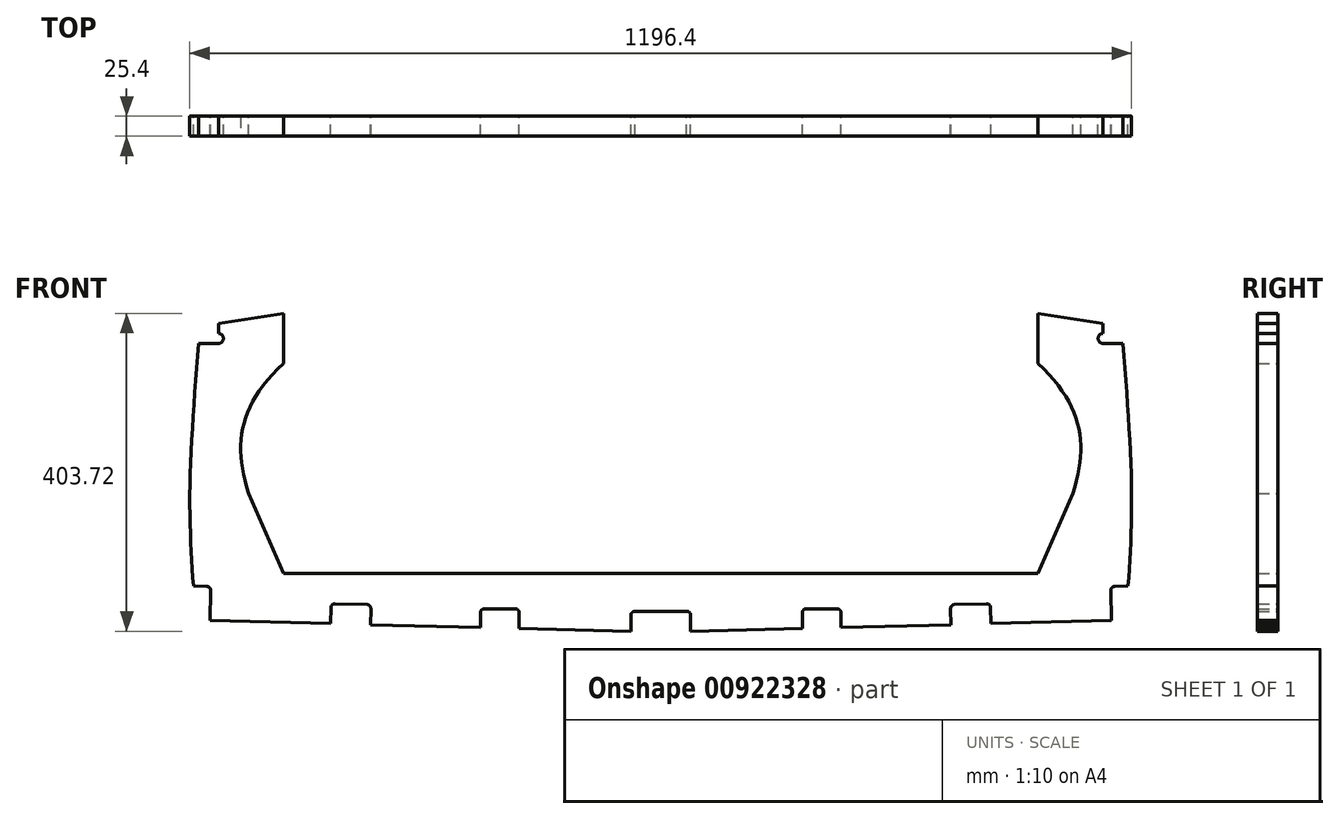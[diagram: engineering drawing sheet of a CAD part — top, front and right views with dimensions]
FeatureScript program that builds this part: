
annotation { "Feature Type Name" : "Feature", "Feature Type Description" : "" }
export const myFeature = defineFeature(function(context is Context, id is Id, definition is map)
    precondition{}
    {
        {
            var Q0;
            Q0=qCreatedBy(makeId("Front.planeOp"),FACE);
            var sketch = newSketch(context, id + "F0", { "sketchPlane" : qUnion([Q0])});
            skLineSegment(sketch, "E0", {"start": v(-38, -73.52) * mm, "end": v(-180.28, -69.8) * mm});
            skLineSegment(sketch, "E1", {"start": v(-180.28, -69.8) * mm, "end": v(-179.77, -50.34) * mm});
            skLineSegment(sketch, "E2", {"start": v(-184.85, -45.12) * mm, "end": v(-224.05, -45.12) * mm});
            skLineSegment(sketch, "E3", {"start": v(-229.13, -50.2) * mm, "end": v(-229.13, -68.9) * mm});
            skLineSegment(sketch, "E4", {"start": v(-229.13, -68.9) * mm, "end": v(-368.78, -65.22) * mm});
            skLineSegment(sketch, "E5", {"start": v(-368.78, -65.22) * mm, "end": v(-368.24, -44.91) * mm});
            skLineSegment(sketch, "E6", {"start": v(-373.19, -39.7) * mm, "end": v(-413.82, -38.63) * mm});
            skLineSegment(sketch, "E7", {"start": v(-419.03, -43.58) * mm, "end": v(-419.56, -63.89) * mm});
            skLineSegment(sketch, "E8", {"start": v(-572.7, -59.86) * mm, "end": v(-571.7, -21.77) * mm});
            skLineSegment(sketch, "E9", {"start": v(-576.65, -16.56) * mm, "end": v(-593.66, -16.11) * mm});
            skLineSegment(sketch, "E10", {"start": v(-561.9, 317.5) * mm, "end": v(-479.35, 330.2) * mm});
            skLineSegment(sketch, "E11", {"start": v(-479.35, 330.2) * mm, "end": v(-479.35, 266.6) * mm});
            skLineSegment(sketch, "E12", {"start": v(-479.35, 0) * mm, "end": v(-523.8, 101.6) * mm});
            skLineSegment(sketch, "E13", {"start": v(-561.9, 292.1) * mm, "end": v(-587.3, 292.1) * mm});
            skFitSpline(sketch, "E14", {"points": [v(-479.35, 266.6) * mm, v(-523.8, 101.6) * mm], "startDerivative": vector(-173.65, -164.2) * mm, "endDerivative": vector(56.39, -189.22) * mm});
            skLineSegment(sketch, "E15", {"start": v(-479.35, 0) * mm, "end": v(0, 0) * mm});
            skLineSegment(sketch, "E16", {"start": v(-572.7, -59.86) * mm, "end": v(-419.56, -63.89) * mm});
            skFitSpline(sketch, "E17", {"points": [v(-593.66, -16.11) * mm, v(-598.16, 100.95) * mm, v(-587.3, 292.1) * mm], "startDerivative": vector(-16.76, 250.48) * mm, "endDerivative": vector(27.67, 361.42) * mm});
            skPoint(sketch, "E18.visualSharp", {"position": v(-571.57, -16.7) * mm});
            skArc(sketch, "E18.filletArc", {"start": v(-571.7, -21.77) * mm, "mid": v(-573.1, -18.14) * mm, "end": v(-576.65, -16.56) * mm});
            skPoint(sketch, "E19.visualSharp", {"position": v(-418.9, -38.5) * mm});
            skArc(sketch, "E19.filletArc", {"start": v(-413.82, -38.63) * mm, "mid": v(-417.45, -40.02) * mm, "end": v(-419.03, -43.58) * mm});
            skPoint(sketch, "E20.visualSharp", {"position": v(-368.11, -39.83) * mm});
            skArc(sketch, "E20.filletArc", {"start": v(-368.24, -44.91) * mm, "mid": v(-369.64, -41.28) * mm, "end": v(-373.19, -39.7) * mm});
            skPoint(sketch, "E21.visualSharp", {"position": v(-229.13, -45.12) * mm});
            skArc(sketch, "E21.filletArc", {"start": v(-224.05, -45.12) * mm, "mid": v(-227.64, -46.61) * mm, "end": v(-229.13, -50.2) * mm});
            skLineSegment(sketch, "E22", {"start": v(-561.9, 317.5) * mm, "end": v(-561.9, 304.8) * mm});
            skLineSegment(sketch, "E23.MirrorCS", {"start": v(576.65, -16.56) * mm, "end": v(593.66, -16.11) * mm});
            skArc(sketch, "E24.MirrorCS", {"start": v(571.7, -21.77) * mm, "mid": v(573.1, -18.14) * mm, "end": v(576.65, -16.56) * mm});
            skLineSegment(sketch, "E25.MirrorCS", {"start": v(561.9, 317.5) * mm, "end": v(561.9, 304.8) * mm});
            skArc(sketch, "E26.MirrorCS", {"start": v(413.82, -38.63) * mm, "mid": v(417.45, -40.02) * mm, "end": v(419.03, -43.58) * mm});
            skArc(sketch, "E27.MirrorCS", {"start": v(368.24, -44.91) * mm, "mid": v(369.64, -41.28) * mm, "end": v(373.19, -39.7) * mm});
            skArc(sketch, "E28.MirrorCS", {"start": v(224.05, -45.12) * mm, "mid": v(227.64, -46.61) * mm, "end": v(229.13, -50.2) * mm});
            skLineSegment(sketch, "E29.MirrorCS", {"start": v(180.28, -69.8) * mm, "end": v(179.77, -50.34) * mm});
            skLineSegment(sketch, "E30.MirrorCS", {"start": v(368.78, -65.22) * mm, "end": v(368.24, -44.91) * mm});
            skLineSegment(sketch, "E31.MirrorCS", {"start": v(561.9, 292.1) * mm, "end": v(587.3, 292.1) * mm});
            skLineSegment(sketch, "E32.MirrorCS", {"start": v(419.03, -43.58) * mm, "end": v(419.56, -63.89) * mm});
            skLineSegment(sketch, "E33.MirrorCS", {"start": v(229.13, -50.2) * mm, "end": v(229.13, -68.9) * mm});
            skLineSegment(sketch, "E34.MirrorCS", {"start": v(373.19, -39.7) * mm, "end": v(413.82, -38.63) * mm});
            skLineSegment(sketch, "E35.MirrorCS", {"start": v(184.85, -45.12) * mm, "end": v(224.05, -45.12) * mm});
            skLineSegment(sketch, "E36.MirrorCS", {"start": v(572.7, -59.86) * mm, "end": v(419.56, -63.89) * mm});
            skLineSegment(sketch, "E37.MirrorCS", {"start": v(561.9, 317.5) * mm, "end": v(479.35, 330.2) * mm});
            skPoint(sketch, "E38.MirrorP", {"position": v(229.13, -45.12) * mm});
            skLineSegment(sketch, "E39.MirrorCS", {"start": v(229.13, -68.9) * mm, "end": v(368.78, -65.22) * mm});
            skLineSegment(sketch, "E40.MirrorCS", {"start": v(479.35, 330.2) * mm, "end": v(479.35, 266.6) * mm});
            skPoint(sketch, "E41.MirrorP", {"position": v(571.57, -16.7) * mm});
            skPoint(sketch, "E42.MirrorP", {"position": v(368.11, -39.83) * mm});
            skLineSegment(sketch, "E43.MirrorCS", {"start": v(479.35, 0) * mm, "end": v(0, 0) * mm});
            skLineSegment(sketch, "E44.MirrorCS", {"start": v(479.35, 0) * mm, "end": v(523.8, 101.6) * mm});
            skLineSegment(sketch, "E45.MirrorCS", {"start": v(572.7, -59.86) * mm, "end": v(571.7, -21.77) * mm});
            skLineSegment(sketch, "E46.MirrorCS", {"start": v(38, -73.52) * mm, "end": v(180.28, -69.8) * mm});
            skFitSpline(sketch, "E47.MirrorCS", {"points": [v(479.35, 266.6) * mm, v(523.8, 101.6) * mm], "startDerivative": vector(173.65, -164.2) * mm, "endDerivative": vector(-56.39, -189.22) * mm});
            skFitSpline(sketch, "E48.MirrorCS", {"points": [v(593.66, -16.11) * mm, v(598.16, 100.95) * mm, v(587.3, 292.1) * mm], "startDerivative": vector(16.76, 250.48) * mm, "endDerivative": vector(-27.67, 361.42) * mm});
            skPoint(sketch, "E49.MirrorP", {"position": v(418.9, -38.5) * mm});
            skArc(sketch, "E50", {"start": v(561.9, 304.8) * mm, "mid": v(555.55, 298.45) * mm, "end": v(561.9, 292.1) * mm});
            skArc(sketch, "E51", {"start": v(-561.9, 292.1) * mm, "mid": v(-555.55, 298.45) * mm, "end": v(-561.9, 304.8) * mm});
            skPoint(sketch, "E52.visualSharp", {"position": v(-179.63, -45.12) * mm});
            skArc(sketch, "E52.filletArc", {"start": v(-179.77, -50.34) * mm, "mid": v(-181.2, -46.66) * mm, "end": v(-184.85, -45.12) * mm});
            skPoint(sketch, "E53.visualSharp", {"position": v(179.63, -45.12) * mm});
            skArc(sketch, "E53.filletArc", {"start": v(184.85, -45.12) * mm, "mid": v(181.2, -46.66) * mm, "end": v(179.77, -50.34) * mm});
            skLineSegment(sketch, "E54", {"start": v(-38, -73.52) * mm, "end": v(-38, -53.4) * mm});
            skLineSegment(sketch, "E55", {"start": v(38, -73.52) * mm, "end": v(38, -53.2) * mm});
            skPoint(sketch, "E56.visualSharp", {"position": v(-38, -48.15) * mm});
            skArc(sketch, "E56.filletArc", {"start": v(-32.5, -48.33) * mm, "mid": v(-36.36, -49.65) * mm, "end": v(-38, -53.4) * mm});
            skPoint(sketch, "E57.visualSharp", {"position": v(38, -48.15) * mm});
            skArc(sketch, "E57.filletArc", {"start": v(38, -53.2) * mm, "mid": v(36.35, -49.47) * mm, "end": v(32.48, -48.15) * mm});
            skLineSegment(sketch, "E58", {"start": v(-32.5, -48.33) * mm, "end": v(32.48, -48.15) * mm});
            skSolve(sketch);
        }
        {
            var Q0;
            Q0=makeQuery(id+"F0.imprint","IMPRINT",FACE,{"disambiguationData":[TD([[makeQuery(id+"F0.imprint","IMPRINT",EDGE,{"derivedFrom":sQuery(id+"F0.wireOp",EDGE,"E0")}),-1.0]])]});
            extrude(context, id + "F1", {"entities" : qUnion([Q0]), "depth" : 25.4 * mm, "offsetDistance" : 25.4 * mm});
        }
    });
